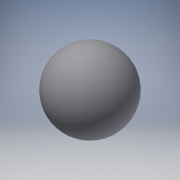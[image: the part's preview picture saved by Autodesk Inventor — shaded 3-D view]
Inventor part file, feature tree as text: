
AUTODESK INVENTOR PART (.ipt)
format: ipt  version: 2016 (Build 200138000, 138)  size: 116,224 bytes
history: native  units: in
note: dims shown in document units (in); Inventor stores cm internally (conversion verified against a paired STEP export)
features: revolve x1, sketch x1
ambient origin geometry x8: Origin, YZ Plane, XZ Plane, XY Plane, X Axis, Y Axis, Z Axis, Center Point
bodies: Solid1 (feature_tree)
feature tree (2):
  revolve  "Revolution1"  Angle=90.0deg
  sketch  "Sketch1"  dims[d0=0.5354in d1=90.0deg]
